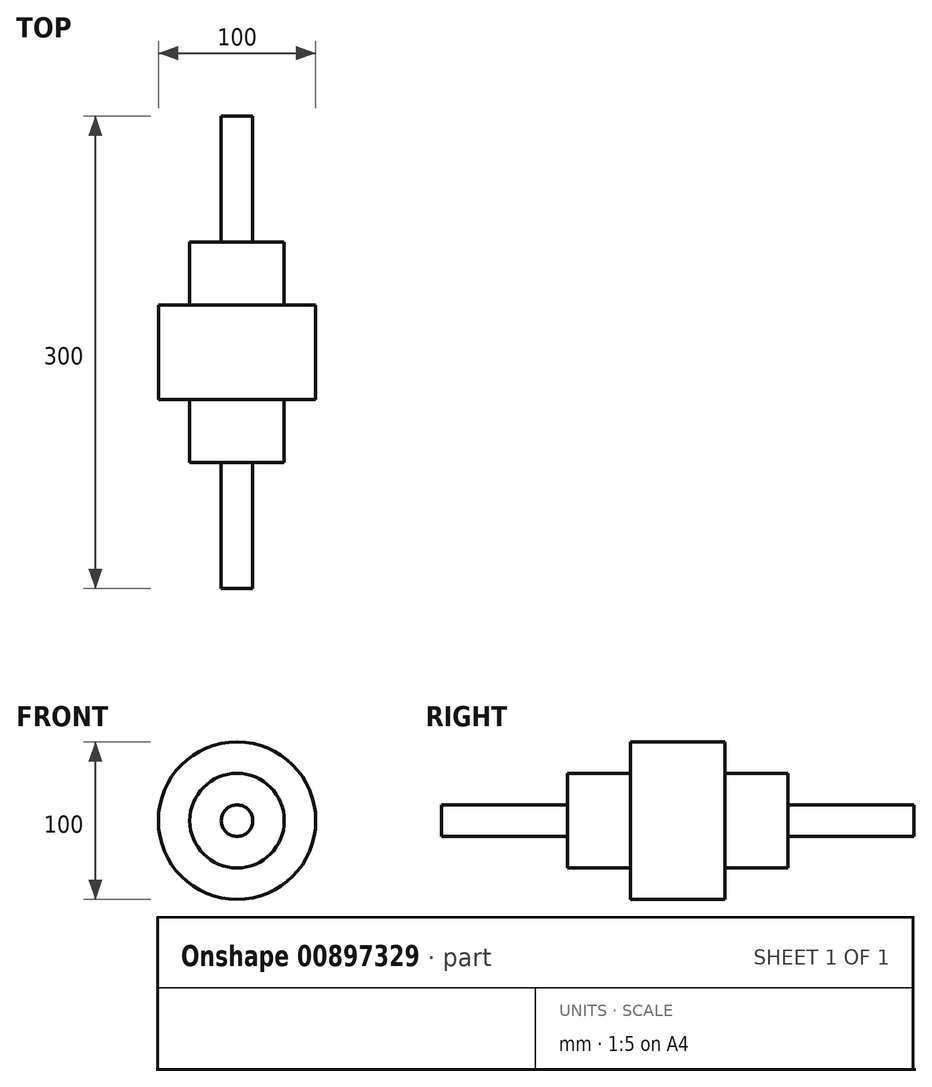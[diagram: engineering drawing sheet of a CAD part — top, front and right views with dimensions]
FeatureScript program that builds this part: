
annotation { "Feature Type Name" : "Feature", "Feature Type Description" : "" }
export const myFeature = defineFeature(function(context is Context, id is Id, definition is map)
    precondition{}
    {
        {
            var Q0;
            Q0=qCreatedBy(makeId("Front.planeOp"),FACE);
            var sketch = newSketch(context, id + "F0", { "sketchPlane" : qUnion([Q0])});
            skCircle(sketch, "E0", {"center": v(0, 0) * mm, "radius": 50 * mm});
            skSolve(sketch);
        }
        {
            var Q0;
            Q0=makeQuery(id+"F0.imprint","IMPRINT",FACE,{"disambiguationData":[TD([[makeQuery(id+"F0.imprint","IMPRINT",EDGE,{"derivedFrom":sQuery(id+"F0.wireOp",EDGE,"E0")}),1.0]])]});
            extrude(context, id + "F1", {"entities" : qUnion([Q0]), "depth" : 30 * mm, "offsetDistance" : 25.4 * mm});
        }
        {
            var Q0;
            Q0=makeQuery(id+"F1.opExtrude","CAP_FACE",FACE,{"disambiguationData":[OSD([sQuery(id+"F0.wireOp",EDGE,"E0")])],"isStart":true});
            extrude(context, id + "F2", {"entities" : qUnion([Q0]), "operationType" : NewBodyOperationType.ADD, "depth" : 30 * mm, "offsetDistance" : 25.4 * mm});
        }
        {
            var Q0;
            Q0=makeQuery(id+"F2.opExtrude","CAP_FACE",FACE,{"disambiguationData":[OSD([sQuery(id+"F0.wireOp",EDGE,"E0")])],"isStart":false});
            var sketch = newSketch(context, id + "F3", { "sketchPlane" : qUnion([Q0])});
            skCircle(sketch, "E1", {"center": v(0, 0) * mm, "radius": 30 * mm});
            skSolve(sketch);
        }
        {
            var Q0;
            Q0=makeQuery(id+"F3.imprint","IMPRINT",FACE,{"disambiguationData":[TD([[makeQuery(id+"F3.imprint","IMPRINT",EDGE,{"derivedFrom":sQuery(id+"F3.wireOp",EDGE,"E1")}),1.0]])]});
            extrude(context, id + "F4", {"entities" : qUnion([Q0]), "operationType" : NewBodyOperationType.ADD, "depth" : 40 * mm, "offsetDistance" : 25.4 * mm});
        }
        {
            var Q0;
            Q0=makeQuery(id+"F1.opExtrude","CAP_FACE",FACE,{"disambiguationData":[OSD([sQuery(id+"F0.wireOp",EDGE,"E0")])],"isStart":false});
            var sketch = newSketch(context, id + "F5", { "sketchPlane" : qUnion([Q0])});
            skCircle(sketch, "E2", {"center": v(0, 0) * mm, "radius": 30 * mm});
            skSolve(sketch);
        }
        {
            var Q0;
            Q0=makeQuery(id+"F5.imprint","IMPRINT",FACE,{"disambiguationData":[TD([[makeQuery(id+"F5.imprint","IMPRINT",EDGE,{"derivedFrom":sQuery(id+"F5.wireOp",EDGE,"E2")}),1.0]])]});
            extrude(context, id + "F6", {"entities" : qUnion([Q0]), "operationType" : NewBodyOperationType.ADD, "depth" : 40 * mm, "offsetDistance" : 25.4 * mm});
        }
        {
            var Q0;
            Q0=makeQuery(id+"F6.opExtrude","CAP_FACE",FACE,{"disambiguationData":[OSD([sQuery(id+"F5.wireOp",EDGE,"E2")])],"isStart":false});
            var sketch = newSketch(context, id + "F7", { "sketchPlane" : qUnion([Q0])});
            skCircle(sketch, "E3", {"center": v(0, 0) * mm, "radius": 10 * mm});
            skSolve(sketch);
        }
        {
            var Q0;
            Q0=makeQuery(id+"F7.imprint","IMPRINT",FACE,{"disambiguationData":[TD([[makeQuery(id+"F7.imprint","IMPRINT",EDGE,{"derivedFrom":sQuery(id+"F7.wireOp",EDGE,"E3")}),1.0]])]});
            extrude(context, id + "F8", {"entities" : qUnion([Q0]), "operationType" : NewBodyOperationType.ADD, "depth" : 80 * mm, "offsetDistance" : 25.4 * mm});
        }
        {
            var Q0;
            Q0=makeQuery(id+"F4.opExtrude","CAP_FACE",FACE,{"disambiguationData":[OSD([sQuery(id+"F3.wireOp",EDGE,"E1")])],"isStart":false});
            var sketch = newSketch(context, id + "F9", { "sketchPlane" : qUnion([Q0])});
            skCircle(sketch, "E4", {"center": v(0, 0) * mm, "radius": 10 * mm});
            skSolve(sketch);
        }
        {
            var Q0;
            Q0=makeQuery(id+"F9.imprint","IMPRINT",FACE,{"disambiguationData":[TD([[makeQuery(id+"F9.imprint","IMPRINT",EDGE,{"derivedFrom":sQuery(id+"F9.wireOp",EDGE,"E4")}),1.0]])]});
            extrude(context, id + "F10", {"entities" : qUnion([Q0]), "operationType" : NewBodyOperationType.ADD, "depth" : 80 * mm, "offsetDistance" : 25.4 * mm});
        }
    });
